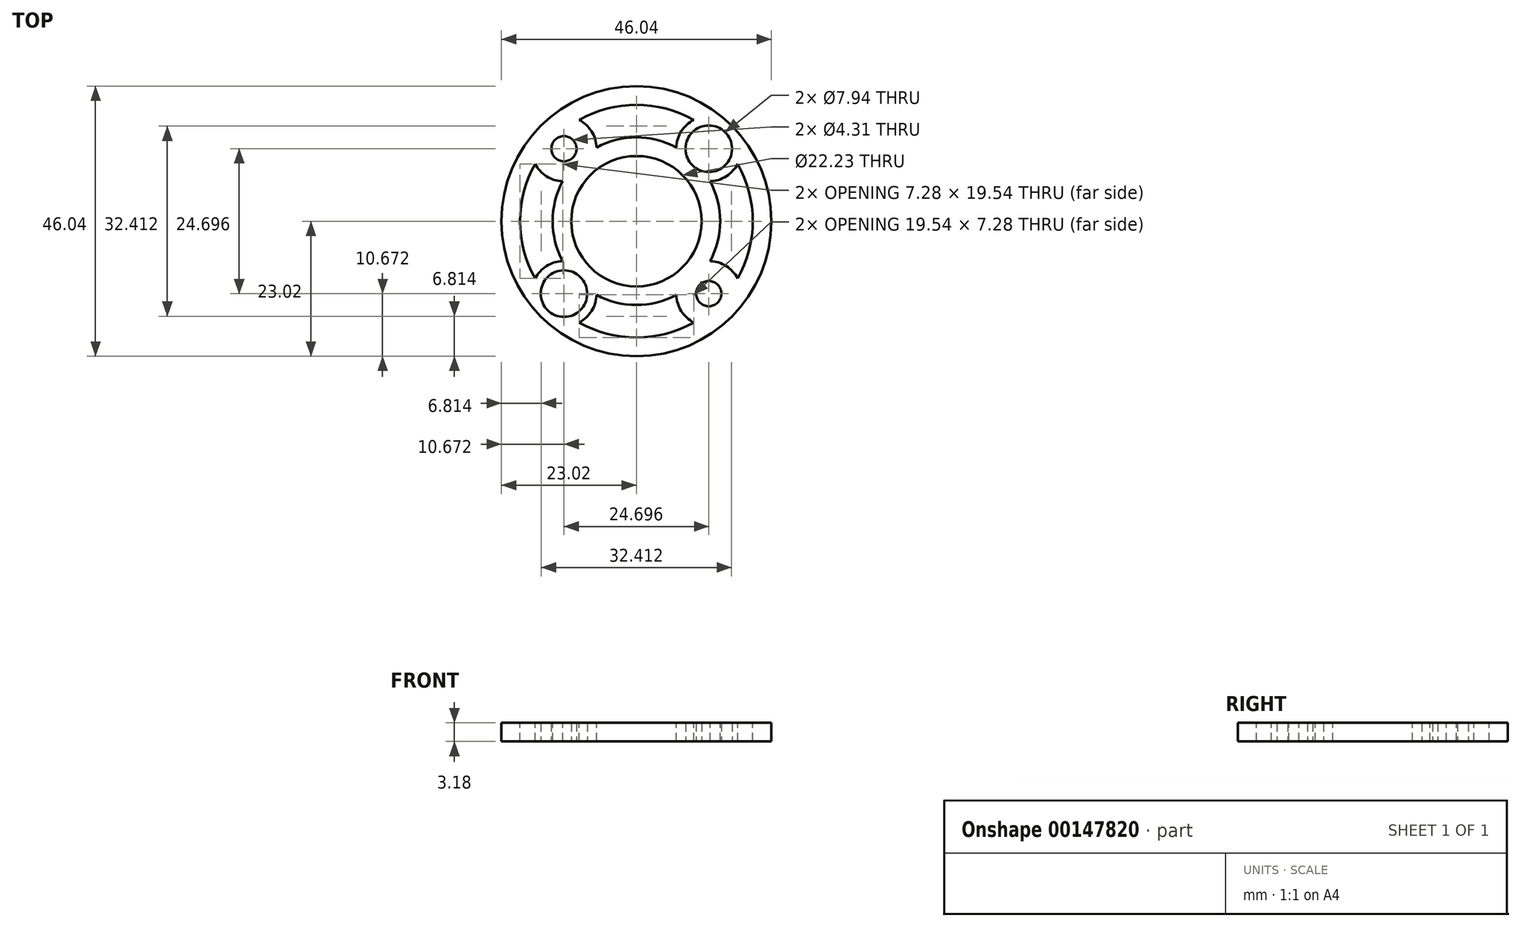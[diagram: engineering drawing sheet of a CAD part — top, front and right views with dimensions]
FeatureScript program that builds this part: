
annotation { "Feature Type Name" : "Feature", "Feature Type Description" : "" }
export const myFeature = defineFeature(function(context is Context, id is Id, definition is map)
    precondition{}
    {
        {
            var Q0;
            Q0=qCreatedBy(makeId("Top.planeOp"),FACE);
            var sketch = newSketch(context, id + "F0", { "sketchPlane" : qUnion([Q0])});
            skCircle(sketch, "E0", {"center": v(0, 0) * mm, "radius": 23.02 * mm});
            skCircle(sketch, "E1", {"center": v(0, 0) * mm, "radius": 11.11 * mm});
            skLineSegment(sketch, "E2.bottom", {"start": v(-12.35, 12.35) * mm, "end": v(12.35, 12.35) * mm, "construction": true});
            skLineSegment(sketch, "E2.top", {"start": v(-12.35, -12.35) * mm, "end": v(12.35, -12.35) * mm, "construction": true});
            skLineSegment(sketch, "E2.left", {"start": v(-12.35, 12.35) * mm, "end": v(-12.35, -12.35) * mm, "construction": true});
            skLineSegment(sketch, "E2.right", {"start": v(12.35, 12.35) * mm, "end": v(12.35, -12.35) * mm, "construction": true});
            skCircle(sketch, "E3", {"center": v(12.35, 12.35) * mm, "radius": 3.97 * mm});
            skCircle(sketch, "E4", {"center": v(-12.35, 12.35) * mm, "radius": 2.15 * mm});
            skCircle(sketch, "E5", {"center": v(-12.35, -12.35) * mm, "radius": 3.97 * mm});
            skCircle(sketch, "E6", {"center": v(12.35, -12.35) * mm, "radius": 2.15 * mm});
            skSolve(sketch);
        }
        {
            var Q0;
            Q0=qSketchRegion(id+"F0",true);
            extrude(context, id + "F1", {"entities" : qUnion([Q0]), "depth" : 3.17 * mm});
        }
        {
            var Q0;
            Q0=makeQuery(id+"F1.opExtrude","CAP_FACE",FACE,{"disambiguationData":[OSD([sQuery(id+"F0.wireOp",EDGE,"E0"),sQuery(id+"F0.wireOp",EDGE,"E1"),sQuery(id+"F0.wireOp",EDGE,"E3"),sQuery(id+"F0.wireOp",EDGE,"E4"),sQuery(id+"F0.wireOp",EDGE,"E5"),sQuery(id+"F0.wireOp",EDGE,"E6")])],"isStart":false});
            var sketch = newSketch(context, id + "F2", { "sketchPlane" : qUnion([Q0])});
            skArc(sketch, "E7", {"start": v(-6.8, 12.57) * mm, "mid": v(-7.65, 15.32) * mm, "end": v(-9.77, 17.27) * mm});
            skArc(sketch, "E8", {"start": v(9.77, 17.27) * mm, "mid": v(7.65, 15.32) * mm, "end": v(6.8, 12.57) * mm});
            skArc(sketch, "E9", {"start": v(6.8, 12.57) * mm, "mid": v(0, 14.29) * mm, "end": v(-6.8, 12.57) * mm});
            skArc(sketch, "E10", {"start": v(9.77, 17.27) * mm, "mid": v(0, 19.84) * mm, "end": v(-9.77, 17.27) * mm});
            skArc(sketch, "E11", {"start": v(-17.27, 9.77) * mm, "mid": v(-15.32, 7.65) * mm, "end": v(-12.57, 6.8) * mm});
            skArc(sketch, "E12", {"start": v(-12.57, 6.8) * mm, "mid": v(-14.29, 0) * mm, "end": v(-12.57, -6.8) * mm});
            skArc(sketch, "E13", {"start": v(-12.57, -6.8) * mm, "mid": v(-15.32, -7.65) * mm, "end": v(-17.27, -9.77) * mm});
            skArc(sketch, "E14", {"start": v(-17.27, 9.77) * mm, "mid": v(-19.84, 0) * mm, "end": v(-17.27, -9.77) * mm});
            skArc(sketch, "E15", {"start": v(12.57, 6.8) * mm, "mid": v(15.32, 7.65) * mm, "end": v(17.27, 9.77) * mm});
            skArc(sketch, "E16", {"start": v(17.27, -9.77) * mm, "mid": v(19.84, 0) * mm, "end": v(17.27, 9.77) * mm});
            skArc(sketch, "E17", {"start": v(12.57, -6.8) * mm, "mid": v(14.29, 0) * mm, "end": v(12.57, 6.8) * mm});
            skArc(sketch, "E18", {"start": v(17.27, -9.77) * mm, "mid": v(15.32, -7.65) * mm, "end": v(12.57, -6.8) * mm});
            skArc(sketch, "E19", {"start": v(-9.77, -17.27) * mm, "mid": v(-7.65, -15.32) * mm, "end": v(-6.8, -12.57) * mm});
            skArc(sketch, "E20", {"start": v(6.8, -12.57) * mm, "mid": v(7.65, -15.32) * mm, "end": v(9.77, -17.27) * mm});
            skArc(sketch, "E21", {"start": v(-6.8, -12.57) * mm, "mid": v(0, -14.29) * mm, "end": v(6.8, -12.57) * mm});
            skArc(sketch, "E22", {"start": v(-9.77, -17.27) * mm, "mid": v(0, -19.84) * mm, "end": v(9.77, -17.27) * mm});
            skSolve(sketch);
        }
        {
            var Q0;
            Q0=qSketchRegion(id+"F2",true);
            var Q1;
            Q1=makeQuery(id+"F1.opExtrude","CAP_FACE",FACE,{"disambiguationData":[OSD([sQuery(id+"F0.wireOp",EDGE,"E0"),sQuery(id+"F0.wireOp",EDGE,"E1"),sQuery(id+"F0.wireOp",EDGE,"E3"),sQuery(id+"F0.wireOp",EDGE,"E4"),sQuery(id+"F0.wireOp",EDGE,"E5"),sQuery(id+"F0.wireOp",EDGE,"E6")])],"isStart":true});
            extrude(context, id + "F3", {"entities" : qUnion([Q0]), "operationType" : NewBodyOperationType.REMOVE, "endBound" : BoundingType.UP_TO_SURFACE, "oppositeDirection" : true, "endBoundEntityFace" : qUnion([Q1]), "depth" : 25.4 * mm});
        }
    });
